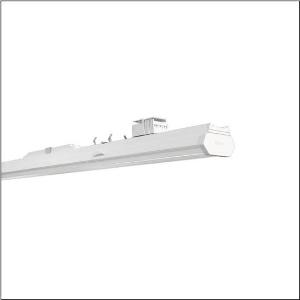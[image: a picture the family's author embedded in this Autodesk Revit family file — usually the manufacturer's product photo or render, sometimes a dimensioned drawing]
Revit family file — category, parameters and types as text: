
# Revit family: licross_r__11_protected_ho_51td12dn4fxm3s_901f
name_source: partatom
category: Lighting Fixtures
units: mm (PartAtom-declared; Revit-internal decimal feet)

## family parameters
Cut with Voids When Loaded = No
Host = Face
Light Source = No
Part Type = Normal
Room Calculation Point = No
Round Connector Dimension = Use Diameter
Shared = No

## types (1)
- --- (1 x LED, 970 lm, 7.4 W, 4000K)
    Apparent Load = 7 VA
    CIE Flux Codes = 70 91 97 98 100
    Color Rendering = 80
    Color Temperature = 4000K
    Default Elevation = 1800 mm
    Description = Licross® 11 Protected HO, luminaire insert, of sheet steel, galvanised, coil coated, white, length: 1.500mm, width: 90mm, height: 101mm, LED rated luminous flux: 15.270lm, light colour: 840, control gear: DALI 2, with plug, 6-pole, with phase selection, for trunking rail, 14-core, mains connection: 220..240V, AC, 50/60Hz, rated input power: 91W, for trunking rail, 14-core, halogen-free wiring, for emergency light function, converter,control gear: single battery element, battery: LiFeP04, 9Ah, primary light control with lens, of plastic, primary optical cover: cover, of PMMA, light emission: direct distribution, primary light characteristic: symmetric, protection rating (complete): IP54, insulation class (complete): insulation class I (protective earthing), certification: CE, UKCA, protection symbol: D if used in an environment with non-conductive dust loads with corresponding accessories, impact resistance: IK06, permissible ambient temperature for indoor applications: +5..+30°C, standard: EN 60598-2-22, LABS conformity tested according to VDMA 24364:2018-05, reducing of maximum allowable ambient temperature of 5°C with ceiling mounting, corresponds to IFS (International Featured Standards) requirements for safety and quality in the food industry, packaging unit: 1 piece
    Height = 92 mm
    Lamp = 1 x LED
    Lamp Light Flux = 970 lm
    Lamp Power = 7.4 W
    Lamp count = 1
    Length = 1500 mm
    Luminous efficacy = 131 lm/W
    Manufacturer = Siteco
    ModVariant = No
    Model = 51TD12DN4FXM3S
    Mounting Place = Ceiling
    Mounting Type = Pendant
    Number of Poles = 1
    OnlyDefault = Yes
    Power Factor = 1
    Product Name = Licross® 11 Protected HO
    Product group = luminaire insert
    ProductGroupID = 901
    Protection Class = Protection class I
    Protection Degree = IP 54
    RLX_Detail_Level = 1
    RLX_Emergency_Light_Flux = 0 lm
    RLX_Emergency_Type = 0
    RLX_Emergency_Type_DB = No
    RlxData = <blob elided: 24905 chars, md5=64f5a6bb>
    Socket = socket
    Standby Power = 0 W
    System Light Flux = 970 lm
    System Power = 7 W
    Type Comments = : emergency light operation: 3 h
    Type Image = l_1256145.jpg
    URL = http://relux.com
    VarID = @adj_041569
    Voltage = 0 V
    Weight = 0.00 kg
    Width = 88 mm

## geometry (parser evidence)
native form markers: Blend x4, Sweep x10
no freeform markers — native parametric forms only
